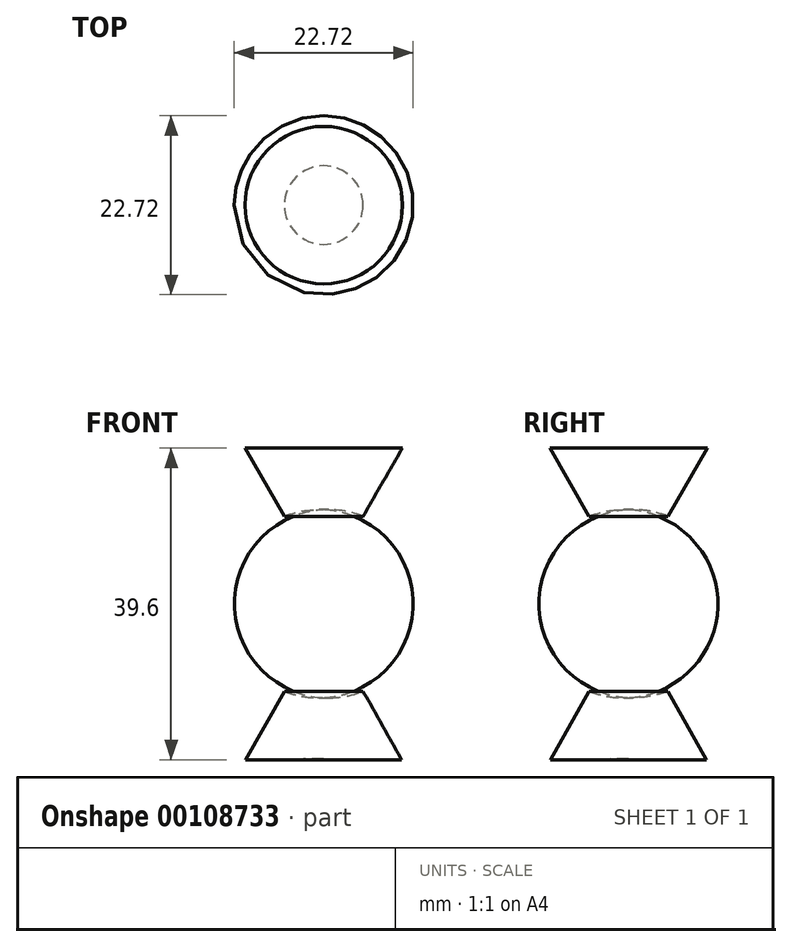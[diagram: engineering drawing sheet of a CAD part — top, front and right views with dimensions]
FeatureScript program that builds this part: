
annotation { "Feature Type Name" : "Feature", "Feature Type Description" : "" }
export const myFeature = defineFeature(function(context is Context, id is Id, definition is map)
    precondition{}
    {
        {
            var Q0;
            Q0=qCreatedBy(makeId("Front.planeOp"),FACE);
            var sketch = newSketch(context, id + "F0", { "sketchPlane" : qUnion([Q0])});
            skLineSegment(sketch, "E0", {"start": v(0, 21.48) * mm, "end": v(0, -18.52) * mm});
            skLineSegment(sketch, "E1", {"start": v(0, 21.48) * mm, "end": v(-10, 21.48) * mm});
            skLineSegment(sketch, "E2", {"start": v(0.1, -18) * mm, "end": v(-9.9, -18.12) * mm});
            skLineSegment(sketch, "E3", {"start": v(-10, 21.48) * mm, "end": v(-5, 12.81) * mm});
            skLineSegment(sketch, "E4", {"start": v(-9.9, -18.12) * mm, "end": v(-5, -9.4) * mm});
            skArc(sketch, "E5", {"start": v(-5, 12.81) * mm, "mid": v(-12.54, 1.7) * mm, "end": v(-5, -9.4) * mm});
            skSolve(sketch);
        }
        {
            var Q0;
            {var subQ4=sQuery(id+"F0.wireOp",EDGE,"E1");Q0=makeQuery(id+"F0.imprint","IMPRINT",FACE,{"disambiguationData":[TD([[makeQuery(id+"F0.imprint","IMPRINT",EDGE,{"derivedFrom":subQ4}),1.0]])]});}
            var Q1;
            Q1=sQuery(id+"F0.wireOp",EDGE,"E0");
            revolve(context, id + "F1", {"entities" : qUnion([Q0]), "axis" : qUnion([Q1]), "revolveType" : RevolveType.FULL});
        }
    });
